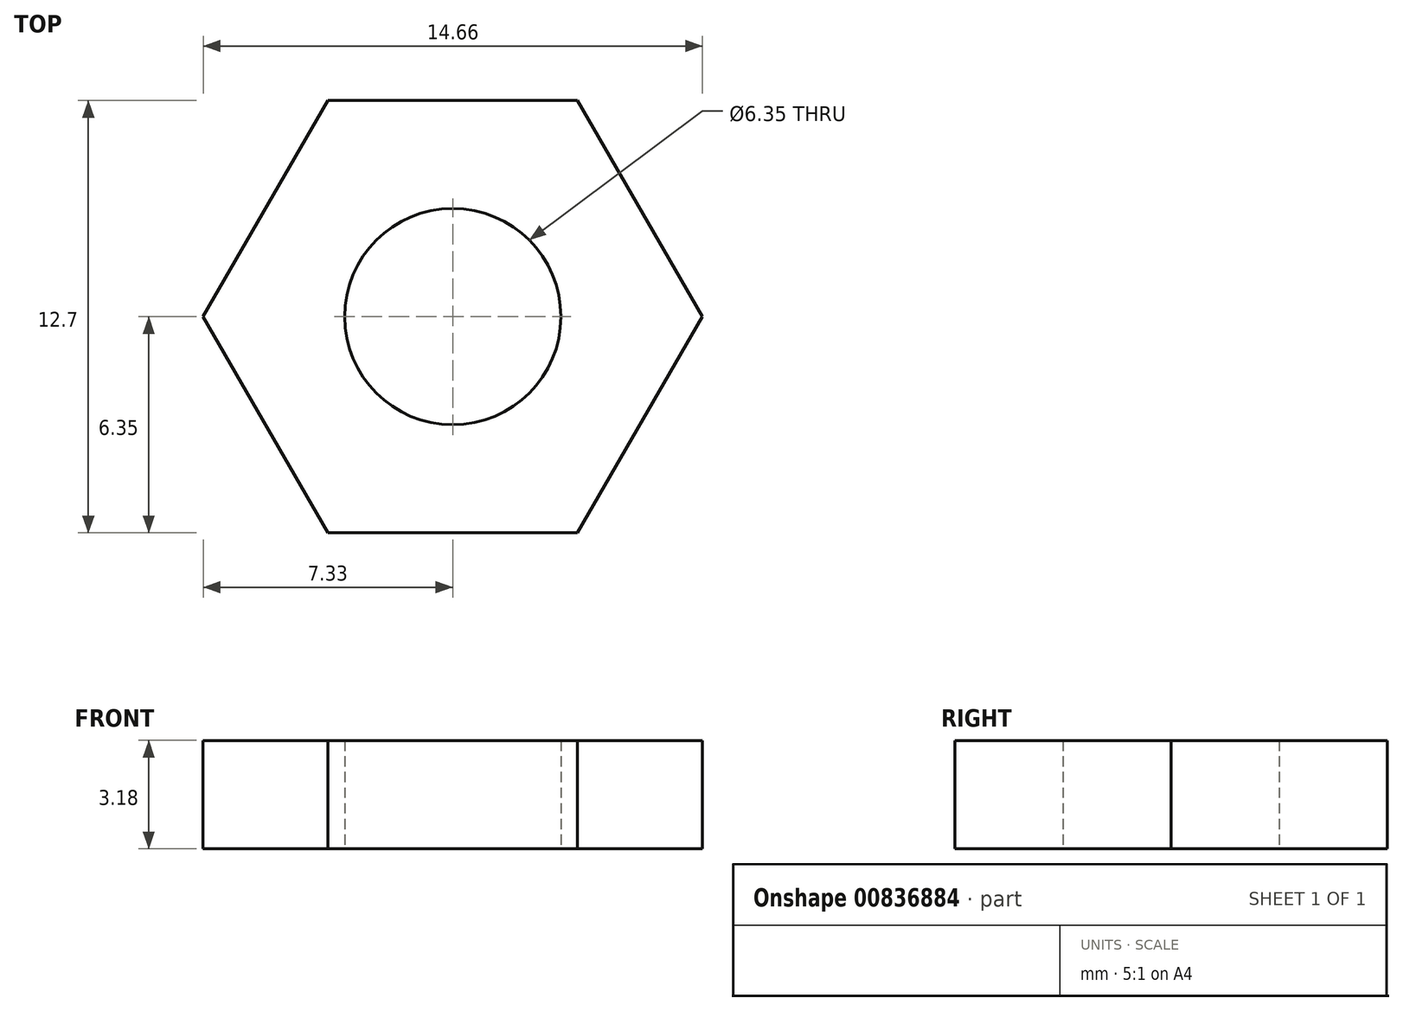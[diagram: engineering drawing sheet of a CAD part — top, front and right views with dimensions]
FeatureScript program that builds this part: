
annotation { "Feature Type Name" : "Feature", "Feature Type Description" : "" }
export const myFeature = defineFeature(function(context is Context, id is Id, definition is map)
    precondition{}
    {
        {
            var Q0;
            Q0=qCreatedBy(makeId("Top.planeOp"),FACE);
            var sketch = newSketch(context, id + "F0", { "sketchPlane" : qUnion([Q0])});
            skCircle(sketch, "E0", {"center": v(0, 0) * mm, "radius": 3.18 * mm});
            skCircle(sketch, "E1.cCircle", {"center": v(0, 0) * mm, "radius": 6.35 * mm, "construction": true});
            skLineSegment(sketch, "E1.0", {"start": v(-7.33, 0) * mm, "end": v(-3.67, 6.35) * mm});
            skLineSegment(sketch, "E1.1", {"start": v(-3.67, 6.35) * mm, "end": v(3.67, 6.35) * mm});
            skLineSegment(sketch, "E1.2", {"start": v(3.67, 6.35) * mm, "end": v(7.33, 0) * mm});
            skLineSegment(sketch, "E1.3", {"start": v(7.33, 0) * mm, "end": v(3.67, -6.35) * mm});
            skLineSegment(sketch, "E1.4", {"start": v(3.67, -6.35) * mm, "end": v(-3.67, -6.35) * mm});
            skLineSegment(sketch, "E1.5", {"start": v(-3.67, -6.35) * mm, "end": v(-7.33, 0) * mm});
            skPoint(sketch, "E1.0.midPoint", {"position": v(-5.5, 3.18) * mm});
            skSolve(sketch);
        }
        {
            var Q0;
            Q0 = qSketchRegion(id + "F0", true);
            extrude(context, id + "F1", {"entities" : qUnion([Q0]), "depth" : 3.17 * mm, "offsetDistance" : 25.4 * mm});
        }
    });
